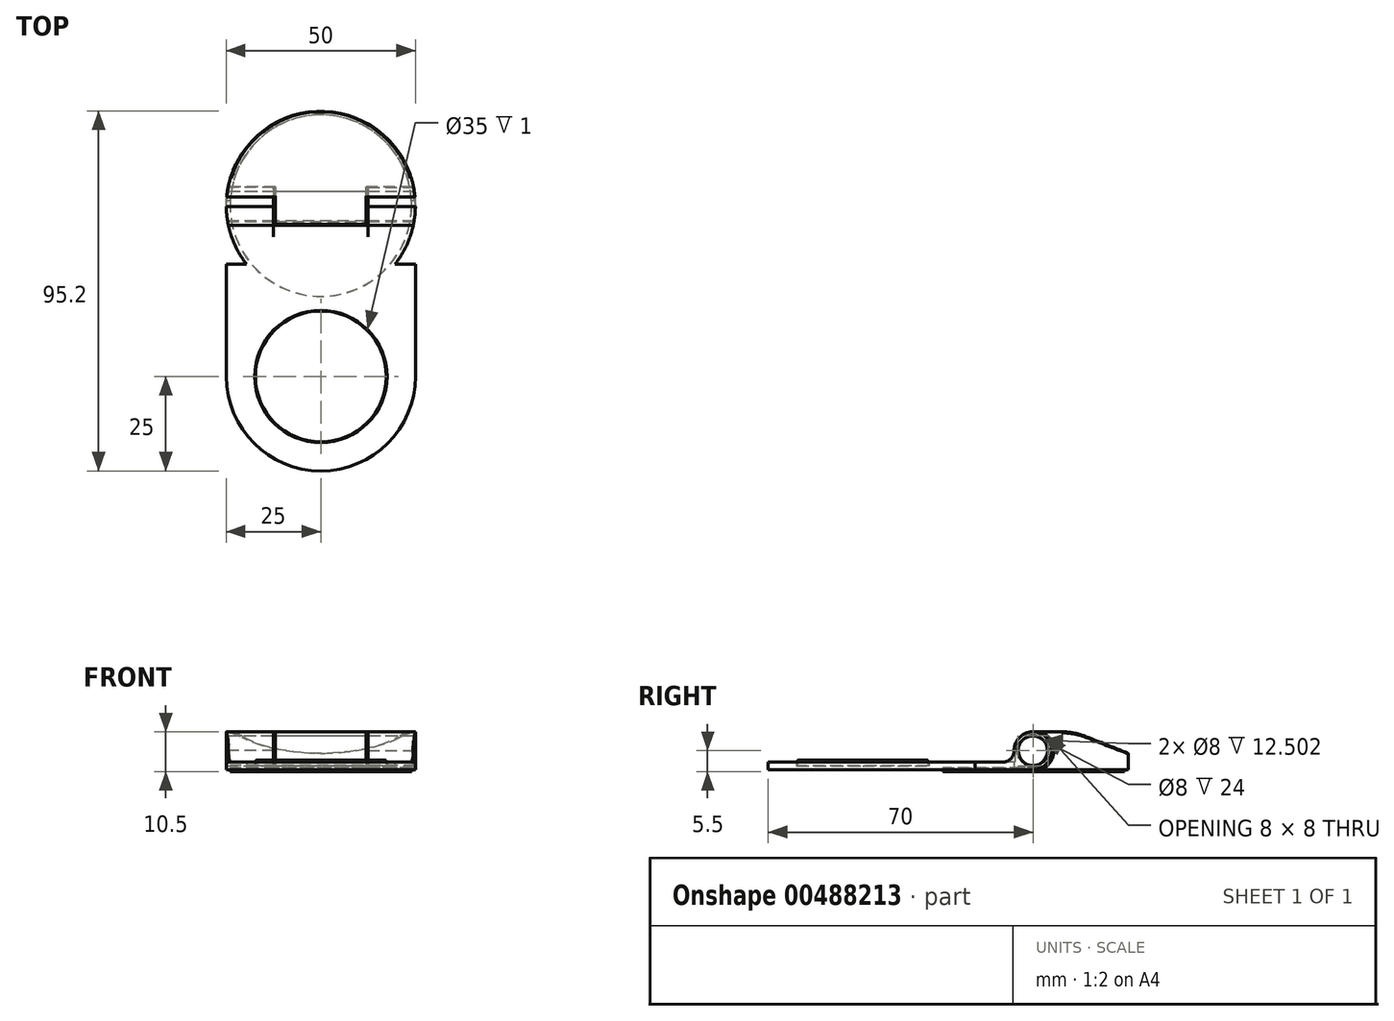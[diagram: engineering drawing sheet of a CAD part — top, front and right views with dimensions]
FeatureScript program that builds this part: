
annotation { "Feature Type Name" : "Feature", "Feature Type Description" : "" }
export const myFeature = defineFeature(function(context is Context, id is Id, definition is map)
    precondition{}
    {
        {
            var Q0;
            Q0=qCreatedBy(makeId("Top.planeOp"),FACE);
            var sketch = newSketch(context, id + "F0", { "sketchPlane" : qUnion([Q0])});
            skCircle(sketch, "E0", {"center": v(0, 0) * mm, "radius": 24 * mm});
            skSolve(sketch);
        }
        {
            var Q0;
            Q0 = qSketchRegion(id + "F0", true);
            extrude(context, id + "F1", {"entities" : qUnion([Q0]), "depth" : 1 * mm});
        }
        {
            var Q0;
            Q0=qCreatedBy(makeId("Top.planeOp"),FACE);
            cPlane(context, id + "F2", {"entities" : qUnion([Q0]), "cplaneType" : CPlaneType.OFFSET, "offset" : .5 * mm, "width" : 152.4 * mm, "height" : 152.4 * mm});
        }
        {
            var Q0;
            Q0=qCreatedBy(id+"F2.planeOp",FACE);
            var sketch = newSketch(context, id + "F3", { "sketchPlane" : qUnion([Q0])});
            skCircle(sketch, "E1", {"center": v(0, 0) * mm, "radius": 25 * mm, "construction": true});
            skLineSegment(sketch, "E2", {"start": v(-24.5, 5) * mm, "end": v(24.5, 5) * mm, "construction": true});
            skLineSegment(sketch, "E3", {"start": v(-24.5, -5) * mm, "end": v(24.5, -5) * mm, "construction": true});
            skLineSegment(sketch, "E4", {"start": v(-12, 5) * mm, "end": v(-12, -5) * mm});
            skLineSegment(sketch, "E5", {"start": v(-12, -5) * mm, "end": v(12, -5) * mm});
            skLineSegment(sketch, "E6", {"start": v(12, -5) * mm, "end": v(12, 5) * mm});
            skLineSegment(sketch, "E7", {"start": v(12, 5) * mm, "end": v(24.5, 5) * mm});
            skLineSegment(sketch, "E8", {"start": v(-12, 5) * mm, "end": v(-24.5, 5) * mm});
            skLineSegment(sketch, "E9", {"start": v(-12, 0) * mm, "end": v(-25, 0) * mm, "construction": true});
            skLineSegment(sketch, "E10", {"start": v(12, 0) * mm, "end": v(25, 0) * mm, "construction": true});
            skArc(sketch, "E11", {"start": v(24.5, 5) * mm, "mid": v(0, 25) * mm, "end": v(-24.5, 5) * mm});
            skSolve(sketch);
        }
        {
            var Q0;
            Q0 = qSketchRegion(id + "F3", true);
            extrude(context, id + "F4", {"entities" : qUnion([Q0]), "depth" : 10 * mm});
        }
        {
            var Q0;
            Q0=makeQuery(id+"F4.opExtrude","CAP_EDGE",EDGE,{"disambiguationData":[OSD([sQuery(id+"F3.wireOp",EDGE,"E5")])],"isStart":false});
            fillet(context, id + "F5", {"entities" : qUnion([Q0]), "radius" : 5 * mm, "tangentPropagation" : true, "allowEdgeOverflow" : false});
        }
        {
            var Q0;
            Q0=qCreatedBy(id+"F2.planeOp",FACE);
            var sketch = newSketch(context, id + "F6", { "sketchPlane" : qUnion([Q0])});
            skArc(sketch, "E12", {"start": v(-25, -45.2) * mm, "mid": v(0, -70.2) * mm, "end": v(25, -45.2) * mm});
            skArc(sketch, "E13", {"start": v(-24.53, 4.8) * mm, "mid": v(-24.88, 2.41) * mm, "end": v(-25, 0) * mm});
            skLineSegment(sketch, "E14", {"start": v(25, 0) * mm, "end": v(25, 0) * mm});
            skCircle(sketch, "E15", {"center": v(0, 0) * mm, "radius": 25 * mm, "construction": true});
            skLineSegment(sketch, "E16", {"start": v(-25, 0) * mm, "end": v(-25, -45.2) * mm});
            skLineSegment(sketch, "E17", {"start": v(-24.53, 4.8) * mm, "end": v(-12.5, 4.8) * mm});
            skLineSegment(sketch, "E18", {"start": v(-12.5, 4.8) * mm, "end": v(-12.5, -5.2) * mm});
            skLineSegment(sketch, "E19", {"start": v(-12.5, -5.2) * mm, "end": v(12.5, -5.2) * mm});
            skLineSegment(sketch, "E20", {"start": v(12.5, -5.2) * mm, "end": v(12.5, 4.8) * mm});
            skLineSegment(sketch, "E21", {"start": v(12.5, 4.8) * mm, "end": v(24.53, 4.8) * mm});
            skLineSegment(sketch, "E22", {"start": v(25, -45.2) * mm, "end": v(25, 0) * mm});
            skArc(sketch, "E23", {"start": v(25, 0) * mm, "mid": v(24.88, 2.41) * mm, "end": v(24.53, 4.8) * mm});
            skLineSegment(sketch, "E24", {"start": v(0, -45.2) * mm, "end": v(0, -11.2) * mm, "construction": true});
            skLineSegment(sketch, "E25", {"start": v(0, -11.2) * mm, "end": v(0, -5.2) * mm, "construction": true});
            skCircle(sketch, "E26", {"center": v(0, -45.2) * mm, "radius": 17.5 * mm});
            skLineSegment(sketch, "E27", {"start": v(-12.5, -5.2) * mm, "end": v(-25, -5.2) * mm});
            skLineSegment(sketch, "E28", {"start": v(12.5, -5.2) * mm, "end": v(25, -5.2) * mm});
            skSolve(sketch);
        }
        {
            var Q0;
            Q0=makeQuery(id+"F6.imprint","IMPRINT",FACE,{"disambiguationData":[TD([[makeQuery(id+"F6.imprint","IMPRINT",EDGE,{"derivedFrom":sQuery(id+"F6.wireOp",EDGE,"E20")}),-1.0]])]});
            var Q1;
            {var subQ1=sQuery(id+"F6.wireOp",EDGE,"E13");Q1=makeQuery(id+"F6.imprint","IMPRINT",FACE,{"disambiguationData":[TD([[makeQuery(id+"F6.imprint","IMPRINT",EDGE,{"derivedFrom":subQ1}),1.0]])]});}
            extrude(context, id + "F7", {"entities" : qUnion([Q0, Q1]), "depth" : 10 * mm});
        }
        {
            var Q0;
            {var subQ1=sQuery(id+"F6.wireOp",EDGE,"E13");Q0=makeQuery(id+"F6.imprint","IMPRINT",FACE,{"disambiguationData":[TD([[makeQuery(id+"F6.imprint","IMPRINT",EDGE,{"derivedFrom":subQ1}),1.0]])]});}
            var Q1;
            {var subQ1=sQuery(id+"F6.wireOp",EDGE,"E12");Q1=makeQuery(id+"F6.imprint","IMPRINT",FACE,{"disambiguationData":[TD([[makeQuery(id+"F6.imprint","IMPRINT",EDGE,{"derivedFrom":subQ1}),1.0]])]});}
            var Q2;
            Q2=makeQuery(id+"F6.imprint","IMPRINT",FACE,{"disambiguationData":[TD([[makeQuery(id+"F6.imprint","IMPRINT",EDGE,{"derivedFrom":sQuery(id+"F6.wireOp",EDGE,"E20")}),-1.0]])]});
            extrude(context, id + "F8", {"entities" : qUnion([Q0, Q1, Q2]), "depth" : 2 * mm});
        }
        {
            var Q0;
            Q0=makeQuery(id+"F6.imprint","IMPRINT",FACE,{"disambiguationData":[TD([[makeQuery(id+"F6.imprint","IMPRINT",EDGE,{"derivedFrom":sQuery(id+"F6.wireOp",EDGE,"E26")}),1.0]])]});
            extrude(context, id + "F9", {"entities" : qUnion([Q0]), "operationType" : NewBodyOperationType.ADD, "depth" : 1 * mm});
        }
        {
            var Q0;
            Q0=makeQuery(id+"F9.opExtrude","CAP_FACE",FACE,{"disambiguationData":[OSD([sQuery(id+"F6.wireOp",EDGE,"E26")])],"isStart":false});
            var sketch = newSketch(context, id + "F10", { "sketchPlane" : qUnion([Q0])});
            skCircle(sketch, "E29.0", {"center": v(0, -45.2) * mm, "radius": 17.3 * mm});
            skSolve(sketch);
        }
        {
            var Q0;
            Q0 = qSketchRegion(id + "F10", true);
            extrude(context, id + "F11", {"entities" : qUnion([Q0]), "depth" : 1.5 * mm});
        }
        {
            var Q0;
            Q0=makeQuery(id+"F7.opExtrude","SWEPT_BODY",BODY,{"disambiguationData":[OSD([sQuery(id+"F6.wireOp",EDGE,"E13"),sQuery(id+"F6.wireOp",EDGE,"E16"),sQuery(id+"F6.wireOp",EDGE,"E17"),sQuery(id+"F6.wireOp",EDGE,"E18"),sQuery(id+"F6.wireOp",EDGE,"E27")])]});
            var Q1;
            Q1=makeQuery(id+"F7.opExtrude","SWEPT_BODY",BODY,{"disambiguationData":[OSD([sQuery(id+"F6.wireOp",EDGE,"E20"),sQuery(id+"F6.wireOp",EDGE,"E21"),sQuery(id+"F6.wireOp",EDGE,"E22"),sQuery(id+"F6.wireOp",EDGE,"E23"),sQuery(id+"F6.wireOp",EDGE,"E28")])]});
            var Q2;
            Q2=makeQuery(id+"F8.opExtrude","SWEPT_BODY",BODY,{"disambiguationData":[OSD([sQuery(id+"F6.wireOp",EDGE,"E12"),sQuery(id+"F6.wireOp",EDGE,"E13"),sQuery(id+"F6.wireOp",EDGE,"E16"),sQuery(id+"F6.wireOp",EDGE,"E17"),sQuery(id+"F6.wireOp",EDGE,"E18"),sQuery(id+"F6.wireOp",EDGE,"E19"),sQuery(id+"F6.wireOp",EDGE,"E20"),sQuery(id+"F6.wireOp",EDGE,"E21"),sQuery(id+"F6.wireOp",EDGE,"E22"),sQuery(id+"F6.wireOp",EDGE,"E23"),sQuery(id+"F6.wireOp",EDGE,"E26")])]});
            booleanBodies(context, id + "F12", {"operationType" : BooleanOperationType.UNION, "tools" : qUnion([Q0, Q1, Q2])});
        }
        {
            var Q0;
            Q0=makeQuery(id+"F7.opExtrude","CAP_EDGE",EDGE,{"disambiguationData":[OSD([sQuery(id+"F6.wireOp",EDGE,"E27")])],"isStart":false});
            var Q1;
            Q1=makeQuery(id+"F7.opExtrude","CAP_EDGE",EDGE,{"disambiguationData":[OSD([sQuery(id+"F6.wireOp",EDGE,"E28")])],"isStart":false});
            fillet(context, id + "F13", {"entities" : qUnion([Q0, Q1]), "radius" : 5 * mm, "tangentPropagation" : true, "allowEdgeOverflow" : false});
        }
        {
            var Q0;
            Q0=makeQuery(id+"F12.opBoolean","INTERSECT",EDGE,{"derivedFrom":[makeQuery(id+"F7.opExtrude","SWEPT_FACE",FACE,{"disambiguationData":[OSD([sQuery(id+"F6.wireOp",EDGE,"E27")])]}),makeQuery(id+"F8.opExtrude","CAP_FACE",FACE,{"disambiguationData":[OSD([sQuery(id+"F6.wireOp",EDGE,"E12"),sQuery(id+"F6.wireOp",EDGE,"E13"),sQuery(id+"F6.wireOp",EDGE,"E16"),sQuery(id+"F6.wireOp",EDGE,"E17"),sQuery(id+"F6.wireOp",EDGE,"E18"),sQuery(id+"F6.wireOp",EDGE,"E19"),sQuery(id+"F6.wireOp",EDGE,"E20"),sQuery(id+"F6.wireOp",EDGE,"E21"),sQuery(id+"F6.wireOp",EDGE,"E22"),sQuery(id+"F6.wireOp",EDGE,"E23"),sQuery(id+"F6.wireOp",EDGE,"E26")])],"isStart":false})]});
            var Q1;
            Q1=makeQuery(id+"F12.opBoolean","INTERSECT",EDGE,{"derivedFrom":[makeQuery(id+"F7.opExtrude","SWEPT_FACE",FACE,{"disambiguationData":[OSD([sQuery(id+"F6.wireOp",EDGE,"E28")])]}),makeQuery(id+"F8.opExtrude","CAP_FACE",FACE,{"disambiguationData":[OSD([sQuery(id+"F6.wireOp",EDGE,"E12"),sQuery(id+"F6.wireOp",EDGE,"E13"),sQuery(id+"F6.wireOp",EDGE,"E16"),sQuery(id+"F6.wireOp",EDGE,"E17"),sQuery(id+"F6.wireOp",EDGE,"E18"),sQuery(id+"F6.wireOp",EDGE,"E19"),sQuery(id+"F6.wireOp",EDGE,"E20"),sQuery(id+"F6.wireOp",EDGE,"E21"),sQuery(id+"F6.wireOp",EDGE,"E22"),sQuery(id+"F6.wireOp",EDGE,"E23"),sQuery(id+"F6.wireOp",EDGE,"E26")])],"isStart":false})]});
            fillet(context, id + "F14", {"entities" : qUnion([Q0, Q1]), "radius" : 3 * mm, "tangentPropagation" : true, "allowEdgeOverflow" : false});
        }
        {
            var Q0;
            Q0=qCreatedBy(makeId("Right.planeOp"),FACE);
            var sketch = newSketch(context, id + "F15", { "sketchPlane" : qUnion([Q0])});
            skLineSegment(sketch, "E30", {"start": v(7.37, 11.78) * mm, "end": v(26.94, 4.08) * mm});
            skLineSegment(sketch, "E31", {"start": v(26.94, 4.08) * mm, "end": v(26.94, 12.28) * mm});
            skLineSegment(sketch, "E32", {"start": v(26.94, 12.28) * mm, "end": v(7.37, 11.78) * mm});
            skSolve(sketch);
        }
        {
            var Q0;
            Q0 = qSketchRegion(id + "F15", true);
            extrude(context, id + "F16", {"entities" : qUnion([Q0]), "operationType" : NewBodyOperationType.REMOVE, "endBound" : BoundingType.SYMMETRIC, "oppositeDirection" : true, "depth" : 76.2 * mm});
        }
        {
            var Q0;
            Q0=makeQuery(id+"F7.opExtrude","CAP_EDGE",EDGE,{"disambiguationData":[OSD([sQuery(id+"F6.wireOp",EDGE,"E21")])],"isStart":false});
            var Q1;
            Q1=makeQuery(id+"F7.opExtrude","CAP_EDGE",EDGE,{"disambiguationData":[OSD([sQuery(id+"F6.wireOp",EDGE,"E21")])],"isStart":true});
            var Q2;
            Q2=makeQuery(id+"F7.opExtrude","CAP_EDGE",EDGE,{"disambiguationData":[OSD([sQuery(id+"F6.wireOp",EDGE,"E17")])],"isStart":false});
            var Q3;
            Q3=makeQuery(id+"F7.opExtrude","CAP_EDGE",EDGE,{"disambiguationData":[OSD([sQuery(id+"F6.wireOp",EDGE,"E17")])],"isStart":true});
            fillet(context, id + "F17", {"entities" : qUnion([Q0, Q1, Q2, Q3]), "radius" : 5.08 * mm, "tangentPropagation" : true, "allowEdgeOverflow" : false});
        }
        {
            var Q0;
            Q0=qCreatedBy(makeId("Right.planeOp"),FACE);
            var sketch = newSketch(context, id + "F18", { "sketchPlane" : qUnion([Q0])});
            skLineSegment(sketch, "E33.0", {"start": v(5, 10.5) * mm, "end": v(5, 0.5) * mm, "construction": true});
            skLineSegment(sketch, "E34", {"start": v(5, 10.5) * mm, "end": v(1.27, 10.5) * mm});
            skLineSegment(sketch, "E35", {"start": v(5, 0.5) * mm, "end": v(1.27, 0.5) * mm});
            skArc(sketch, "E36", {"start": v(1.27, 0.5) * mm, "mid": v(4.98, 5.5) * mm, "end": v(1.27, 10.5) * mm});
            skArc(sketch, "E37", {"start": v(5, 0.5) * mm, "mid": v(6.05, 5.5) * mm, "end": v(5, 10.5) * mm});
            skSolve(sketch);
        }
        {
            var Q0;
            Q0 = qSketchRegion(id + "F18", true);
            extrude(context, id + "F19", {"entities" : qUnion([Q0]), "operationType" : NewBodyOperationType.ADD, "endBound" : BoundingType.SYMMETRIC, "depth" : 52 * mm});
        }
        {
            var Q0;
            Q0=qCreatedBy(id+"F2.planeOp",FACE);
            var sketch = newSketch(context, id + "F20", { "sketchPlane" : qUnion([Q0])});
            skCircle(sketch, "E38", {"center": v(0, 0) * mm, "radius": 25 * mm, "construction": true});
            skLineSegment(sketch, "E39", {"start": v(19.6, -15.52) * mm, "end": v(49.11, -15.52) * mm});
            skLineSegment(sketch, "E40", {"start": v(49.11, -15.52) * mm, "end": v(49.11, 35.45) * mm});
            skLineSegment(sketch, "E41", {"start": v(49.11, 35.45) * mm, "end": v(-49.11, 35.45) * mm});
            skLineSegment(sketch, "E42", {"start": v(-49.11, 35.45) * mm, "end": v(-49.11, -15.52) * mm});
            skLineSegment(sketch, "E43", {"start": v(-49.11, -15.52) * mm, "end": v(-19.6, -15.52) * mm});
            skArc(sketch, "E44", {"start": v(19.6, -15.52) * mm, "mid": v(0, 25) * mm, "end": v(-19.6, -15.52) * mm});
            skSolve(sketch);
        }
        {
            var Q0;
            Q0 = qSketchRegion(id + "F20", true);
            extrude(context, id + "F21", {"entities" : qUnion([Q0]), "operationType" : NewBodyOperationType.REMOVE, "depth" : 25.4 * mm});
        }
        {
            var Q0;
            Q0=makeQuery(id+"F16.boolean.opBoolean","INTERSECT",EDGE,{"derivedFrom":[makeQuery(id+"F4.opExtrude","CAP_FACE",FACE,{"disambiguationData":[OSD([sQuery(id+"F3.wireOp",EDGE,"E4"),sQuery(id+"F3.wireOp",EDGE,"E5"),sQuery(id+"F3.wireOp",EDGE,"E6"),sQuery(id+"F3.wireOp",EDGE,"E7"),sQuery(id+"F3.wireOp",EDGE,"E8"),sQuery(id+"F3.wireOp",EDGE,"E11")])],"isStart":false}),makeQuery(id+"F16.opExtrude","SWEPT_FACE",FACE,{"disambiguationData":[OSD([sQuery(id+"F15.wireOp",EDGE,"E30")])]})]});
            fillet(context, id + "F22", {"entities" : qUnion([Q0]), "radius" : 17.78 * mm, "tangentPropagation" : true, "allowEdgeOverflow" : false});
        }
        {
            var Q0;
            {var subQ0=sQuery(id+"F18.wireOp",EDGE,"E34");var subQ1=sQuery(id+"F18.wireOp",EDGE,"E36");var subQ2=sQuery(id+"F3.wireOp",EDGE,"E4");Q0=makeQuery(id+"F19.boolean.opBoolean","SPLIT",EDGE,{"disambiguationData":[TD([makeQuery(id+"F4.opExtrude","SWEPT_FACE",FACE,{"disambiguationData":[OSD([subQ2])]})])],"derivedFrom":makeQuery(id+"F19.opExtrude","SWEPT_EDGE",EDGE,{"disambiguationData":[OSD([subQ0,subQ1])]})});}
            var Q1;
            {var subQ0=sQuery(id+"F18.wireOp",EDGE,"E36");var subQ1=sQuery(id+"F18.wireOp",EDGE,"E34");var subQ2=sQuery(id+"F3.wireOp",EDGE,"E6");Q1=makeQuery(id+"F19.boolean.opBoolean","SPLIT",EDGE,{"disambiguationData":[TD([makeQuery(id+"F4.opExtrude","SWEPT_FACE",FACE,{"disambiguationData":[OSD([subQ2])]})])],"derivedFrom":makeQuery(id+"F19.opExtrude","SWEPT_EDGE",EDGE,{"disambiguationData":[OSD([subQ1,subQ0])]})});}
            var Q2;
            {var subQ0=sQuery(id+"F18.wireOp",EDGE,"E35");var subQ1=sQuery(id+"F18.wireOp",EDGE,"E36");var subQ2=sQuery(id+"F3.wireOp",EDGE,"E4");Q2=makeQuery(id+"F19.boolean.opBoolean","SPLIT",EDGE,{"disambiguationData":[TD([makeQuery(id+"F4.opExtrude","SWEPT_FACE",FACE,{"disambiguationData":[OSD([subQ2])]})])],"derivedFrom":makeQuery(id+"F19.opExtrude","SWEPT_EDGE",EDGE,{"disambiguationData":[OSD([subQ0,subQ1])]})});}
            var Q3;
            {var subQ0=sQuery(id+"F18.wireOp",EDGE,"E36");var subQ1=sQuery(id+"F18.wireOp",EDGE,"E35");var subQ2=sQuery(id+"F3.wireOp",EDGE,"E6");Q3=makeQuery(id+"F19.boolean.opBoolean","SPLIT",EDGE,{"disambiguationData":[TD([makeQuery(id+"F4.opExtrude","SWEPT_FACE",FACE,{"disambiguationData":[OSD([subQ2])]})])],"derivedFrom":makeQuery(id+"F19.opExtrude","SWEPT_EDGE",EDGE,{"disambiguationData":[OSD([subQ1,subQ0])]})});}
            fillet(context, id + "F23", {"entities" : qUnion([Q0, Q1, Q2, Q3]), "radius" : 0.25 * mm, "tangentPropagation" : true, "allowEdgeOverflow" : false});
        }
        {
            var Q0;
            Q0=makeQuery(id+"F16.boolean.opBoolean","INTERSECT",EDGE,{"derivedFrom":[makeQuery(id+"F4.opExtrude","SWEPT_FACE",FACE,{"disambiguationData":[OSD([sQuery(id+"F3.wireOp",EDGE,"E11")])]}),makeQuery(id+"F16.opExtrude","SWEPT_FACE",FACE,{"disambiguationData":[OSD([sQuery(id+"F15.wireOp",EDGE,"E30")])]})]});
            var Q1;
            Q1=makeQuery(id+"F7.opExtrude","CAP_EDGE",EDGE,{"disambiguationData":[OSD([sQuery(id+"F6.wireOp",EDGE,"E23")])],"isStart":false});
            fillet(context, id + "F24", {"entities" : qUnion([Q0, Q1]), "radius" : 0.25 * mm, "tangentPropagation" : true, "allowEdgeOverflow" : false});
        }
        {
            var Q0;
            Q0=qCreatedBy(makeId("Right.planeOp"),FACE);
            var sketch = newSketch(context, id + "F25", { "sketchPlane" : qUnion([Q0])});
            skCircle(sketch, "E45", {"center": v(-0.2, 5.5) * mm, "radius": 4 * mm});
            skCircle(sketch, "E46.0", {"center": v(-0.2, 5.5) * mm, "radius": 3.9 * mm, "construction": true});
            skSolve(sketch);
        }
        {
            var Q0;
            Q0 = qSketchRegion(id + "F25", true);
            extrude(context, id + "F26", {"entities" : qUnion([Q0]), "operationType" : NewBodyOperationType.REMOVE, "endBound" : BoundingType.SYMMETRIC, "oppositeDirection" : true, "depth" : 76.2 * mm});
        }
        {
            var Q0;
            Q0=qCreatedBy(makeId("Right.planeOp"),FACE);
            var sketch = newSketch(context, id + "F27", { "sketchPlane" : qUnion([Q0])});
            skCircle(sketch, "E47", {"center": v(-0.22, 5.5) * mm, "radius": 3.9 * mm});
            skSolve(sketch);
        }
        {
            var Q0;
            Q0 = qSketchRegion(id + "F27", true);
            extrude(context, id + "F28", {"entities" : qUnion([Q0]), "endBound" : BoundingType.SYMMETRIC, "depth" : 55 * mm});
        }
        {
            var Q0;
            Q0 = qSketchRegion(id + "F20", true);
            extrude(context, id + "F29", {"entities" : qUnion([Q0]), "operationType" : NewBodyOperationType.REMOVE, "endBound" : BoundingType.SYMMETRIC, "oppositeDirection" : true, "depth" : 76.2 * mm});
        }
        {
            var Q0;
            Q0=makeQuery(id+"F11.opExtrude","CAP_EDGE",EDGE,{"disambiguationData":[OSD([sQuery(id+"F10.wireOp",EDGE,"E29.0")])],"isStart":false});
            fillet(context, id + "F30", {"entities" : qUnion([Q0]), "radius" : .3 * mm, "tangentPropagation" : true, "allowEdgeOverflow" : false});
        }
    });
